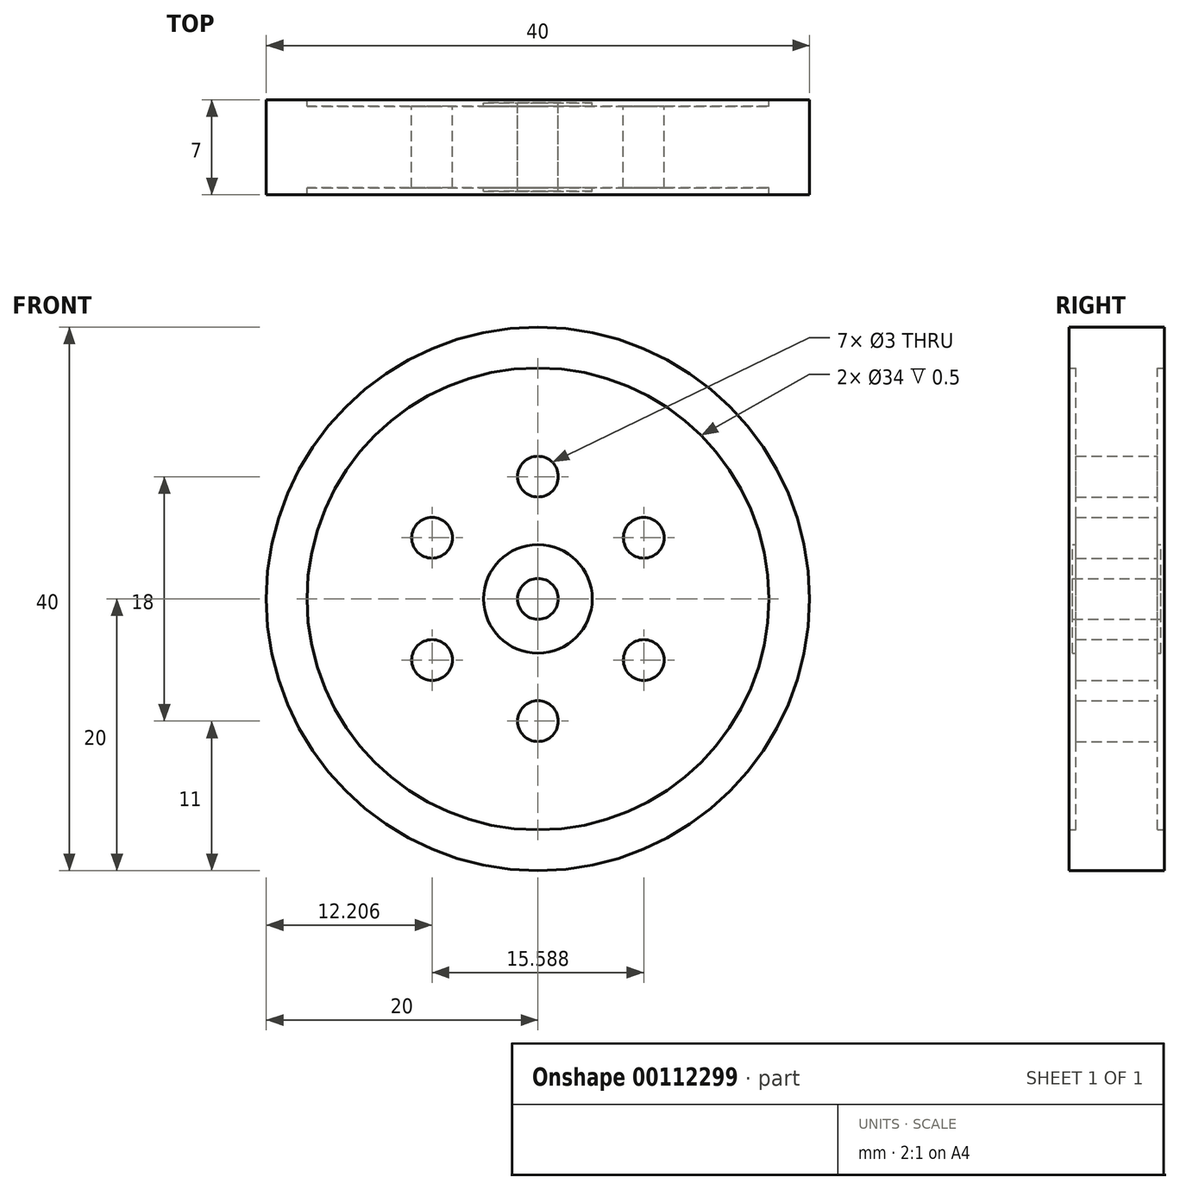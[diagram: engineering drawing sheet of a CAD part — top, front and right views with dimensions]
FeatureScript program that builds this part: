
annotation { "Feature Type Name" : "Feature", "Feature Type Description" : "" }
export const myFeature = defineFeature(function(context is Context, id is Id, definition is map)
    precondition{}
    {
        {
            var Q0;
            Q0=qCreatedBy(makeId("Front.planeOp"),FACE);
            var sketch = newSketch(context, id + "F0", { "sketchPlane" : qUnion([Q0])});
            skCircle(sketch, "E0", {"center": v(0, 0) * mm, "radius": 20 * mm});
            skCircle(sketch, "E1", {"center": v(0, 0) * mm, "radius": 4 * mm});
            skCircle(sketch, "E2", {"center": v(0, 0) * mm, "radius": 1.5 * mm});
            skCircle(sketch, "E3", {"center": v(0, 9) * mm, "radius": 1.5 * mm});
            skCircle(sketch, "E4.1.0", {"center": v(-7.8, 4.5) * mm, "radius": 1.5 * mm});
            skCircle(sketch, "E4.2.0", {"center": v(-7.8, -4.5) * mm, "radius": 1.5 * mm});
            skCircle(sketch, "E4.3.0", {"center": v(0, -9) * mm, "radius": 1.5 * mm});
            skCircle(sketch, "E4.4.0", {"center": v(7.8, -4.5) * mm, "radius": 1.5 * mm});
            skCircle(sketch, "E4.5.0", {"center": v(7.8, 4.5) * mm, "radius": 1.5 * mm});
            skCircle(sketch, "E5", {"center": v(0, 0) * mm, "radius": 17 * mm});
            skSolve(sketch);
        }
        {
            var Q0;
            Q0=makeQuery(id+"F0.imprint","IMPRINT",FACE,{"disambiguationData":[TD([[makeQuery(id+"F0.imprint","IMPRINT",EDGE,{"derivedFrom":sQuery(id+"F0.wireOp",EDGE,"E1")}),1.0]])]});
            extrude(context, id + "F1", {"entities" : qUnion([Q0]), "endBound" : BoundingType.SYMMETRIC, "depth" : 6.5 * mm});
        }
        {
            var Q0;
            Q0=makeQuery(id+"F0.imprint","IMPRINT",FACE,{"disambiguationData":[TD([[makeQuery(id+"F0.imprint","IMPRINT",EDGE,{"derivedFrom":sQuery(id+"F0.wireOp",EDGE,"E1")}),-1.0]])]});
            extrude(context, id + "F2", {"entities" : qUnion([Q0]), "operationType" : NewBodyOperationType.ADD, "endBound" : BoundingType.SYMMETRIC, "depth" : 6 * mm});
        }
        {
            var Q0;
            Q0=qSketchRegion(id+"F0",true);
            extrude(context, id + "F3", {"entities" : qUnion([Q0]), "operationType" : NewBodyOperationType.ADD, "endBound" : BoundingType.SYMMETRIC, "depth" : 7 * mm});
        }
    });
